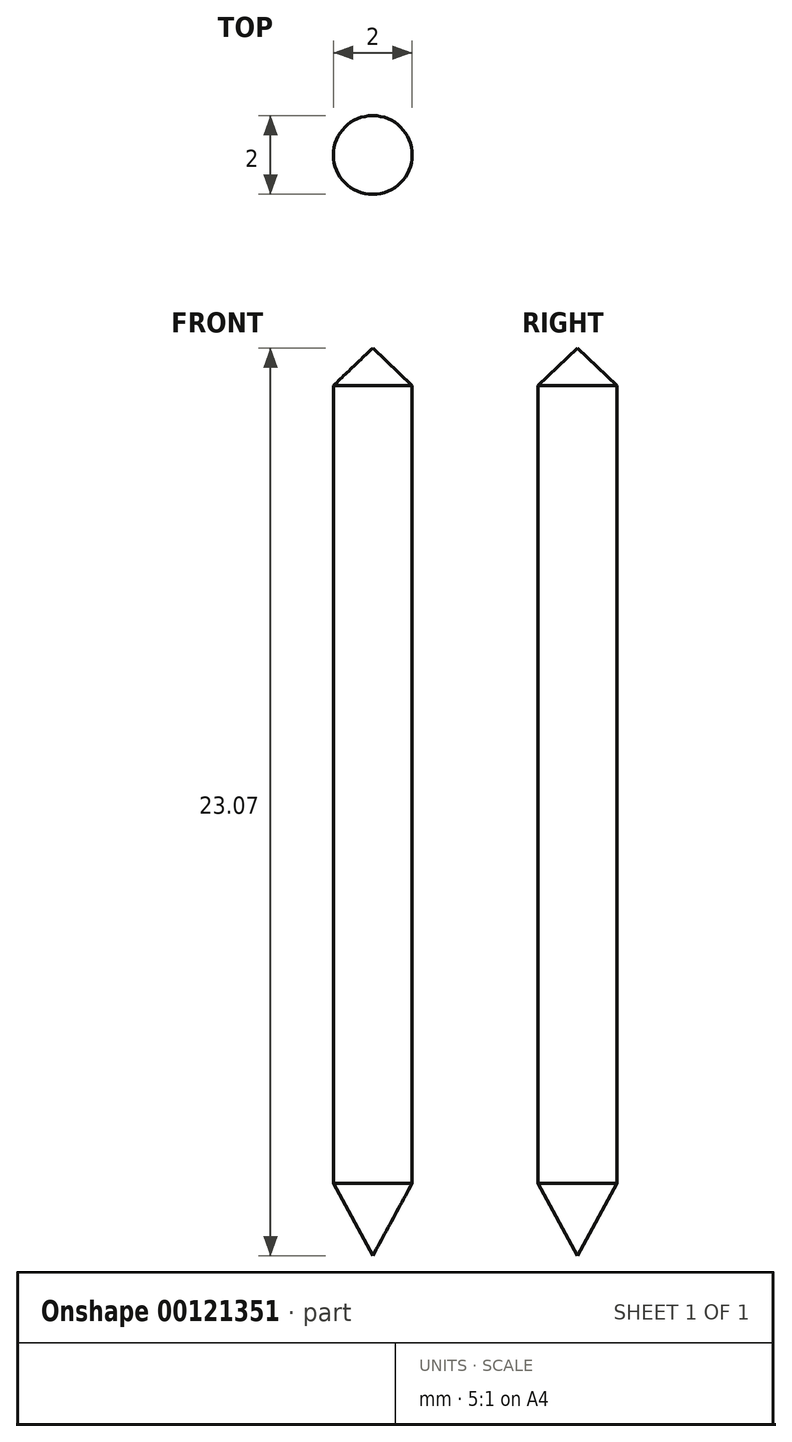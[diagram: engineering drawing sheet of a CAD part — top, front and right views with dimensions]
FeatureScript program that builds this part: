
annotation { "Feature Type Name" : "Feature", "Feature Type Description" : "" }
export const myFeature = defineFeature(function(context is Context, id is Id, definition is map)
    precondition{}
    {
        {
            var Q0;
            Q0=qCreatedBy(makeId("Front.planeOp"),FACE);
            var sketch = newSketch(context, id + "F0", { "sketchPlane" : qUnion([Q0])});
            skLineSegment(sketch, "E0", {"start": v(-7.84, 0) * mm, "end": v(7.53, 0) * mm, "construction": true});
            skLineSegment(sketch, "E1", {"start": v(0, 23.55) * mm, "end": v(0, -11.6) * mm, "construction": true});
            skLineSegment(sketch, "E2.0", {"start": v(-7.84, -11.5) * mm, "end": v(7.53, -11.5) * mm, "construction": true});
            skLineSegment(sketch, "E3.0", {"start": v(-7.84, 10.5) * mm, "end": v(7.53, 10.5) * mm, "construction": true});
            skLineSegment(sketch, "E4.0", {"start": v(-1, 23.55) * mm, "end": v(-1, -11.6) * mm, "construction": true});
            skLineSegment(sketch, "E5", {"start": v(0, 11.46) * mm, "end": v(-1, 10.5) * mm});
            skPoint(sketch, "E5.endSnap0", {"position": v(-0.15, 10.5) * mm});
            skLineSegment(sketch, "E6", {"start": v(-1, 10.5) * mm, "end": v(-1, -9.77) * mm});
            skLineSegment(sketch, "E7", {"start": v(-1, -9.77) * mm, "end": v(0, -11.6) * mm});
            skLineSegment(sketch, "E8", {"start": v(0, 11.46) * mm, "end": v(0, -11.6) * mm});
            skSolve(sketch);
        }
        {
            var Q0;
            Q0=makeQuery(id+"F0.imprint","IMPRINT",FACE,{"disambiguationData":[TD([[makeQuery(id+"F0.imprint","IMPRINT",EDGE,{"derivedFrom":sQuery(id+"F0.wireOp",EDGE,"E5")}),1.0]])]});
            var Q1;
            Q1=sQuery(id+"F0.wireOp",EDGE,"E6");
            var Q2;
            Q2=sQuery(id+"F0.wireOp",EDGE,"E5");
            var Q3;
            Q3=sQuery(id+"F0.wireOp",EDGE,"E7");
            var Q4;
            Q4=sQuery(id+"F0.wireOp",EDGE,"E8");
            revolve(context, id + "F1", {"entities" : qUnion([Q0]), "surfaceEntities" : qUnion([Q1, Q2, Q3]), "axis" : qUnion([Q4]), "revolveType" : RevolveType.FULL});
        }
    });
